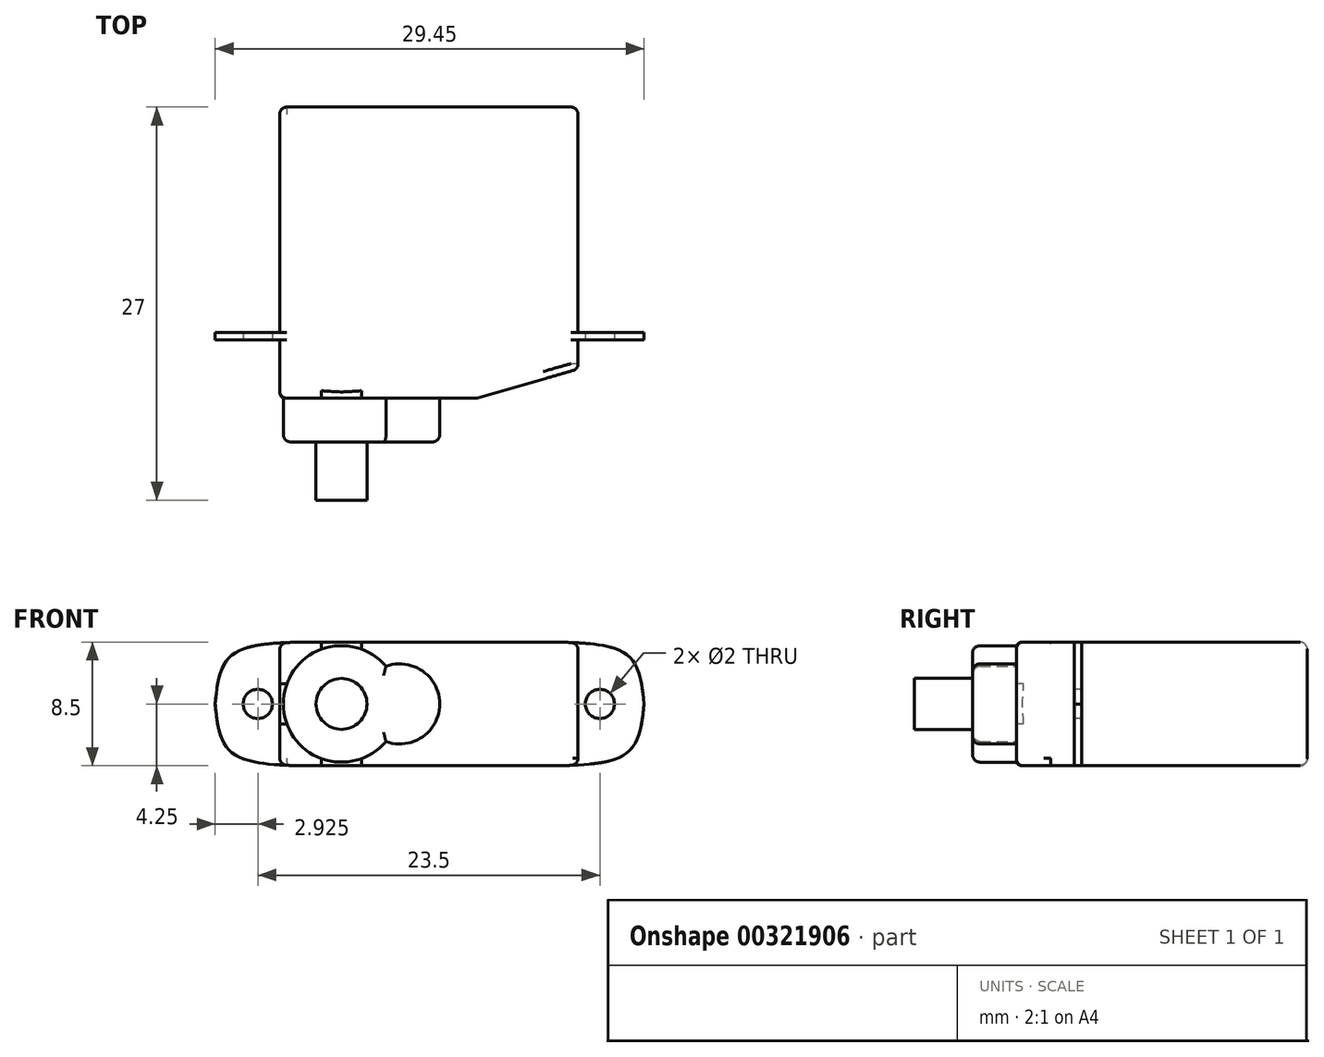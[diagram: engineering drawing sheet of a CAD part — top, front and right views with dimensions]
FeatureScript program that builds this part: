
annotation { "Feature Type Name" : "Feature", "Feature Type Description" : "" }
export const myFeature = defineFeature(function(context is Context, id is Id, definition is map)
    precondition{}
    {
        {
            var Q0;
            Q0=qCreatedBy(makeId("Top.planeOp"),FACE);
            var sketch = newSketch(context, id + "F0", { "sketchPlane" : qUnion([Q0])});
            skLineSegment(sketch, "E0.bottom", {"start": v(-30.64, 3) * mm, "end": v(-10.14, 3) * mm});
            skLineSegment(sketch, "E0.top", {"start": v(-30.64, -17) * mm, "end": v(-17.14, -17) * mm});
            skLineSegment(sketch, "E0.left", {"start": v(-30.64, 3) * mm, "end": v(-30.64, -17) * mm});
            skLineSegment(sketch, "E0.right", {"start": v(-10.14, 3) * mm, "end": v(-10.14, -15) * mm});
            skLineSegment(sketch, "E1", {"start": v(-17.14, -17) * mm, "end": v(-10.14, -15) * mm});
            skLineSegment(sketch, "E2.bottom", {"start": v(-30.64, -13) * mm, "end": v(-35.14, -13) * mm});
            skLineSegment(sketch, "E2.top", {"start": v(-30.64, -12.5) * mm, "end": v(-35.14, -12.5) * mm});
            skLineSegment(sketch, "E2.right", {"start": v(-35.14, -13) * mm, "end": v(-35.14, -12.5) * mm});
            skPoint(sketch, "E3.firstSnap0", {"position": v(-32.9, -12.5) * mm});
            skLineSegment(sketch, "E3.bottom", {"start": v(-10.14, -12.5) * mm, "end": v(-5.54, -12.5) * mm});
            skLineSegment(sketch, "E3.top", {"start": v(-10.14, -13) * mm, "end": v(-5.54, -13) * mm});
            skLineSegment(sketch, "E3.right", {"start": v(-5.54, -12.5) * mm, "end": v(-5.54, -13) * mm});
            skSolve(sketch);
        }
        {
            var Q0;
            {var subQ3=sQuery(id+"F0.wireOp",EDGE,"E0.bottom");Q0=makeQuery(id+"F0.imprint","IMPRINT",FACE,{"disambiguationData":[TD([[makeQuery(id+"F0.imprint","IMPRINT",EDGE,{"derivedFrom":subQ3}),-1.0]])]});}
            var Q1;
            {var subQ0=sQuery(id+"F0.wireOp",EDGE,"E2.bottom");Q1=makeQuery(id+"F0.imprint","IMPRINT",FACE,{"disambiguationData":[TD([[makeQuery(id+"F0.imprint","IMPRINT",EDGE,{"derivedFrom":subQ0}),-1.0]])]});}
            var Q2;
            {var subQ0=sQuery(id+"F0.wireOp",EDGE,"E3.bottom");Q2=makeQuery(id+"F0.imprint","IMPRINT",FACE,{"disambiguationData":[TD([[makeQuery(id+"F0.imprint","IMPRINT",EDGE,{"derivedFrom":subQ0}),-1.0]])]});}
            extrude(context, id + "F1", {"entities" : qUnion([Q0, Q1, Q2]), "depth" : 8.5 * mm});
        }
        {
            var Q0;
            Q0=makeQuery(id+"F1.opExtrude","SWEPT_FACE",FACE,{"disambiguationData":[OSD([sQuery(id+"F0.wireOp",EDGE,"E0.top")])]});
            var sketch = newSketch(context, id + "F2", { "sketchPlane" : qUnion([Q0])});
            skArc(sketch, "E4", {"start": v(-23.34, 6.83) * mm, "mid": v(-30.4, 4.25) * mm, "end": v(-23.34, 1.67) * mm});
            skPoint(sketch, "E4.centerSnap0", {"position": v(-30.64, 4.25) * mm});
            skArc(sketch, "E5", {"start": v(-23.34, 1.67) * mm, "mid": v(-19.64, 4.25) * mm, "end": v(-23.34, 6.83) * mm});
            skSolve(sketch);
        }
        {
            var Q0;
            {var subQ0=sQuery(id+"F2.wireOp",EDGE,"E5");Q0=makeQuery(id+"F2.imprint","IMPRINT",FACE,{"disambiguationData":[TD([[makeQuery(id+"F2.imprint","IMPRINT",EDGE,{"derivedFrom":subQ0}),1.0]])]});}
            extrude(context, id + "F3", {"entities" : qUnion([Q0]), "operationType" : NewBodyOperationType.ADD, "depth" : 3 * mm});
        }
        {
            var Q0;
            Q0=makeQuery(id+"F3.opExtrude","CAP_FACE",FACE,{"disambiguationData":[OSD([sQuery(id+"F2.wireOp",EDGE,"E4"),sQuery(id+"F2.wireOp",EDGE,"E5")])],"isStart":false});
            var sketch = newSketch(context, id + "F4", { "sketchPlane" : qUnion([Q0])});
            skCircle(sketch, "E6", {"center": v(-26.4, 4.25) * mm, "radius": 1.75 * mm});
            skSolve(sketch);
        }
        {
            var Q0;
            Q0=makeQuery(id+"F4.imprint","IMPRINT",FACE,{"disambiguationData":[TD([[makeQuery(id+"F4.imprint","IMPRINT",EDGE,{"derivedFrom":sQuery(id+"F4.wireOp",EDGE,"E6")}),1.0]])]});
            extrude(context, id + "F5", {"entities" : qUnion([Q0]), "operationType" : NewBodyOperationType.ADD, "depth" : 4 * mm});
        }
        {
            var Q0;
            Q0=makeQuery(id+"F1.opExtrude","SWEPT_FACE",FACE,{"disambiguationData":[OSD([sQuery(id+"F0.wireOp",EDGE,"E2.bottom")])]});
            var sketch = newSketch(context, id + "F6", { "sketchPlane" : qUnion([Q0])});
            skCircle(sketch, "E7", {"center": v(-32.14, 4.25) * mm, "radius": 1 * mm});
            skPoint(sketch, "E7.centerSnap0", {"position": v(-35.14, 4.25) * mm});
            skCircle(sketch, "E8", {"center": v(-8.64, 4.25) * mm, "radius": 1 * mm});
            skSolve(sketch);
        }
        {
            var Q0;
            Q0=makeQuery(id+"F6.imprint","IMPRINT",FACE,{"disambiguationData":[TD([[makeQuery(id+"F6.imprint","IMPRINT",EDGE,{"derivedFrom":sQuery(id+"F6.wireOp",EDGE,"E7")}),1.0]])]});
            var Q1;
            Q1=makeQuery(id+"F6.imprint","IMPRINT",FACE,{"disambiguationData":[TD([[makeQuery(id+"F6.imprint","IMPRINT",EDGE,{"derivedFrom":sQuery(id+"F6.wireOp",EDGE,"E8")}),1.0]])]});
            extrude(context, id + "F7", {"entities" : qUnion([Q0, Q1]), "operationType" : NewBodyOperationType.REMOVE, "oppositeDirection" : true, "depth" : 25 * mm});
        }
        {
            var Q0;
            Q0=makeQuery(id+"F1.opExtrude","CAP_EDGE",EDGE,{"disambiguationData":[OSD([sQuery(id+"F0.wireOp",EDGE,"E2.right")])],"isStart":false});
            var Q1;
            Q1=makeQuery(id+"F1.opExtrude","CAP_EDGE",EDGE,{"disambiguationData":[OSD([sQuery(id+"F0.wireOp",EDGE,"E2.right")])],"isStart":true});
            var Q2;
            Q2=makeQuery(id+"F1.opExtrude","CAP_EDGE",EDGE,{"disambiguationData":[OSD([sQuery(id+"F0.wireOp",EDGE,"E3.right")])],"isStart":false});
            var Q3;
            Q3=makeQuery(id+"F1.opExtrude","CAP_EDGE",EDGE,{"disambiguationData":[OSD([sQuery(id+"F0.wireOp",EDGE,"E3.right")])],"isStart":true});
            fillet(context, id + "F8", {"entities" : qUnion([Q0, Q1, Q2, Q3]), "radius" : 7 * mm, "rho" : 0.7, "crossSection" : FilletCrossSection.CONIC, "allowEdgeOverflow" : false});
        }
        {
            var Q0;
            {var subQ0=sQuery(id+"F0.wireOp",EDGE,"E0.left");Q0=makeQuery(id+"F8.opFillet","BLEND_EDGE",EDGE,{"blendedFrom":[makeQuery(id+"F1.opExtrude","CAP_EDGE",EDGE,{"disambiguationData":[OSD([sQuery(id+"F0.wireOp",EDGE,"E2.right")])],"isStart":false}),makeQuery(id+"F1.opExtrude","SWEPT_FACE",FACE,{"disambiguationData":[OSD([subQ0]),TDD([makeQuery(id+"F0.imprint","IMPRINT",EDGE,{"disambiguationData":[TD([[makeQuery(id+"F0.imprint","INTERSECT",VERTEX,{"derivedFrom":[sQuery(id+"F0.wireOp",EDGE,"E0.bottom"),subQ0]}),-1.0]])],"derivedFrom":subQ0})])]})],"blendedInto":[makeQuery(id+"F1.opExtrude","SWEPT_FACE",FACE,{"disambiguationData":[OSD([subQ0]),TDD([makeQuery(id+"F0.imprint","IMPRINT",EDGE,{"disambiguationData":[TD([[makeQuery(id+"F0.imprint","INTERSECT",VERTEX,{"derivedFrom":[sQuery(id+"F0.wireOp",EDGE,"E0.bottom"),subQ0]}),-1.0]])],"derivedFrom":subQ0})])]})]});}
            var Q1;
            {var subQ0=sQuery(id+"F0.wireOp",EDGE,"E0.left");Q1=makeQuery(id+"F8.opFillet","BLEND_EDGE",EDGE,{"blendedFrom":[makeQuery(id+"F1.opExtrude","CAP_EDGE",EDGE,{"disambiguationData":[OSD([sQuery(id+"F0.wireOp",EDGE,"E2.right")])],"isStart":false}),makeQuery(id+"F1.opExtrude","SWEPT_FACE",FACE,{"disambiguationData":[OSD([subQ0]),TDD([makeQuery(id+"F0.imprint","IMPRINT",EDGE,{"disambiguationData":[TD([[makeQuery(id+"F0.imprint","INTERSECT",VERTEX,{"derivedFrom":[sQuery(id+"F0.wireOp",EDGE,"E0.top"),subQ0]}),1.0]])],"derivedFrom":subQ0})])]})],"blendedInto":[makeQuery(id+"F1.opExtrude","SWEPT_FACE",FACE,{"disambiguationData":[OSD([subQ0]),TDD([makeQuery(id+"F0.imprint","IMPRINT",EDGE,{"disambiguationData":[TD([[makeQuery(id+"F0.imprint","INTERSECT",VERTEX,{"derivedFrom":[sQuery(id+"F0.wireOp",EDGE,"E0.top"),subQ0]}),1.0]])],"derivedFrom":subQ0})])]})]});}
            var Q2;
            {var subQ0=sQuery(id+"F0.wireOp",EDGE,"E0.left");Q2=makeQuery(id+"F8.opFillet","BLEND_EDGE",EDGE,{"blendedFrom":[makeQuery(id+"F1.opExtrude","CAP_EDGE",EDGE,{"disambiguationData":[OSD([sQuery(id+"F0.wireOp",EDGE,"E2.right")])],"isStart":true}),makeQuery(id+"F1.opExtrude","SWEPT_FACE",FACE,{"disambiguationData":[OSD([subQ0]),TDD([makeQuery(id+"F0.imprint","IMPRINT",EDGE,{"disambiguationData":[TD([[makeQuery(id+"F0.imprint","INTERSECT",VERTEX,{"derivedFrom":[sQuery(id+"F0.wireOp",EDGE,"E0.top"),subQ0]}),1.0]])],"derivedFrom":subQ0})])]})],"blendedInto":[makeQuery(id+"F1.opExtrude","SWEPT_FACE",FACE,{"disambiguationData":[OSD([subQ0]),TDD([makeQuery(id+"F0.imprint","IMPRINT",EDGE,{"disambiguationData":[TD([[makeQuery(id+"F0.imprint","INTERSECT",VERTEX,{"derivedFrom":[sQuery(id+"F0.wireOp",EDGE,"E0.top"),subQ0]}),1.0]])],"derivedFrom":subQ0})])]})]});}
            var Q3;
            {var subQ0=sQuery(id+"F0.wireOp",EDGE,"E0.left");Q3=makeQuery(id+"F8.opFillet","BLEND_EDGE",EDGE,{"blendedFrom":[makeQuery(id+"F1.opExtrude","CAP_EDGE",EDGE,{"disambiguationData":[OSD([sQuery(id+"F0.wireOp",EDGE,"E2.right")])],"isStart":true}),makeQuery(id+"F1.opExtrude","SWEPT_FACE",FACE,{"disambiguationData":[OSD([subQ0]),TDD([makeQuery(id+"F0.imprint","IMPRINT",EDGE,{"disambiguationData":[TD([[makeQuery(id+"F0.imprint","INTERSECT",VERTEX,{"derivedFrom":[sQuery(id+"F0.wireOp",EDGE,"E0.bottom"),subQ0]}),-1.0]])],"derivedFrom":subQ0})])]})],"blendedInto":[makeQuery(id+"F1.opExtrude","SWEPT_FACE",FACE,{"disambiguationData":[OSD([subQ0]),TDD([makeQuery(id+"F0.imprint","IMPRINT",EDGE,{"disambiguationData":[TD([[makeQuery(id+"F0.imprint","INTERSECT",VERTEX,{"derivedFrom":[sQuery(id+"F0.wireOp",EDGE,"E0.bottom"),subQ0]}),-1.0]])],"derivedFrom":subQ0})])]})]});}
            var Q4;
            Q4=makeQuery(id+"F1.opExtrude","CAP_EDGE",EDGE,{"disambiguationData":[OSD([sQuery(id+"F0.wireOp",EDGE,"E0.bottom")])],"isStart":true});
            var Q5;
            Q5=makeQuery(id+"F1.opExtrude","SWEPT_EDGE",EDGE,{"disambiguationData":[OSD([sQuery(id+"F0.wireOp",EDGE,"E0.bottom"),sQuery(id+"F0.wireOp",EDGE,"E0.left")])]});
            var Q6;
            Q6=makeQuery(id+"F1.opExtrude","CAP_EDGE",EDGE,{"disambiguationData":[OSD([sQuery(id+"F0.wireOp",EDGE,"E0.bottom")])],"isStart":false});
            var Q7;
            Q7=makeQuery(id+"F1.opExtrude","SWEPT_EDGE",EDGE,{"disambiguationData":[OSD([sQuery(id+"F0.wireOp",EDGE,"E0.bottom"),sQuery(id+"F0.wireOp",EDGE,"E0.right")])]});
            var Q8;
            {var subQ0=sQuery(id+"F0.wireOp",EDGE,"E0.right");Q8=makeQuery(id+"F8.opFillet","BLEND_EDGE",EDGE,{"blendedFrom":[makeQuery(id+"F1.opExtrude","CAP_EDGE",EDGE,{"disambiguationData":[OSD([sQuery(id+"F0.wireOp",EDGE,"E3.right")])],"isStart":true}),makeQuery(id+"F1.opExtrude","SWEPT_FACE",FACE,{"disambiguationData":[OSD([subQ0]),TDD([makeQuery(id+"F0.imprint","IMPRINT",EDGE,{"disambiguationData":[TD([[makeQuery(id+"F0.imprint","INTERSECT",VERTEX,{"derivedFrom":[sQuery(id+"F0.wireOp",EDGE,"E0.bottom"),subQ0]}),-1.0]])],"derivedFrom":subQ0})])]})],"blendedInto":[makeQuery(id+"F1.opExtrude","SWEPT_FACE",FACE,{"disambiguationData":[OSD([subQ0]),TDD([makeQuery(id+"F0.imprint","IMPRINT",EDGE,{"disambiguationData":[TD([[makeQuery(id+"F0.imprint","INTERSECT",VERTEX,{"derivedFrom":[sQuery(id+"F0.wireOp",EDGE,"E0.bottom"),subQ0]}),-1.0]])],"derivedFrom":subQ0})])]})]});}
            var Q9;
            {var subQ0=sQuery(id+"F0.wireOp",EDGE,"E0.right");Q9=makeQuery(id+"F8.opFillet","BLEND_EDGE",EDGE,{"blendedFrom":[makeQuery(id+"F1.opExtrude","CAP_EDGE",EDGE,{"disambiguationData":[OSD([sQuery(id+"F0.wireOp",EDGE,"E3.right")])],"isStart":false}),makeQuery(id+"F1.opExtrude","SWEPT_FACE",FACE,{"disambiguationData":[OSD([subQ0]),TDD([makeQuery(id+"F0.imprint","IMPRINT",EDGE,{"disambiguationData":[TD([[makeQuery(id+"F0.imprint","INTERSECT",VERTEX,{"derivedFrom":[sQuery(id+"F0.wireOp",EDGE,"E0.bottom"),subQ0]}),-1.0]])],"derivedFrom":subQ0})])]})],"blendedInto":[makeQuery(id+"F1.opExtrude","SWEPT_FACE",FACE,{"disambiguationData":[OSD([subQ0]),TDD([makeQuery(id+"F0.imprint","IMPRINT",EDGE,{"disambiguationData":[TD([[makeQuery(id+"F0.imprint","INTERSECT",VERTEX,{"derivedFrom":[sQuery(id+"F0.wireOp",EDGE,"E0.bottom"),subQ0]}),-1.0]])],"derivedFrom":subQ0})])]})]});}
            var Q10;
            {var subQ0=sQuery(id+"F0.wireOp",EDGE,"E0.right");Q10=makeQuery(id+"F8.opFillet","BLEND_EDGE",EDGE,{"blendedFrom":[makeQuery(id+"F1.opExtrude","CAP_EDGE",EDGE,{"disambiguationData":[OSD([sQuery(id+"F0.wireOp",EDGE,"E3.right")])],"isStart":false}),makeQuery(id+"F1.opExtrude","SWEPT_FACE",FACE,{"disambiguationData":[OSD([subQ0]),TDD([makeQuery(id+"F0.imprint","IMPRINT",EDGE,{"disambiguationData":[TD([[makeQuery(id+"F0.imprint","INTERSECT",VERTEX,{"derivedFrom":[subQ0,sQuery(id+"F0.wireOp",EDGE,"E1")]}),1.0]])],"derivedFrom":subQ0})])]})],"blendedInto":[makeQuery(id+"F1.opExtrude","SWEPT_FACE",FACE,{"disambiguationData":[OSD([subQ0]),TDD([makeQuery(id+"F0.imprint","IMPRINT",EDGE,{"disambiguationData":[TD([[makeQuery(id+"F0.imprint","INTERSECT",VERTEX,{"derivedFrom":[subQ0,sQuery(id+"F0.wireOp",EDGE,"E1")]}),1.0]])],"derivedFrom":subQ0})])]})]});}
            var Q11;
            {var subQ0=sQuery(id+"F0.wireOp",EDGE,"E0.right");Q11=makeQuery(id+"F8.opFillet","BLEND_EDGE",EDGE,{"blendedFrom":[makeQuery(id+"F1.opExtrude","CAP_EDGE",EDGE,{"disambiguationData":[OSD([sQuery(id+"F0.wireOp",EDGE,"E3.right")])],"isStart":true}),makeQuery(id+"F1.opExtrude","SWEPT_FACE",FACE,{"disambiguationData":[OSD([subQ0]),TDD([makeQuery(id+"F0.imprint","IMPRINT",EDGE,{"disambiguationData":[TD([[makeQuery(id+"F0.imprint","INTERSECT",VERTEX,{"derivedFrom":[subQ0,sQuery(id+"F0.wireOp",EDGE,"E1")]}),1.0]])],"derivedFrom":subQ0})])]})],"blendedInto":[makeQuery(id+"F1.opExtrude","SWEPT_FACE",FACE,{"disambiguationData":[OSD([subQ0]),TDD([makeQuery(id+"F0.imprint","IMPRINT",EDGE,{"disambiguationData":[TD([[makeQuery(id+"F0.imprint","INTERSECT",VERTEX,{"derivedFrom":[subQ0,sQuery(id+"F0.wireOp",EDGE,"E1")]}),1.0]])],"derivedFrom":subQ0})])]})]});}
            var Q12;
            Q12=makeQuery(id+"F1.opExtrude","SWEPT_EDGE",EDGE,{"disambiguationData":[OSD([sQuery(id+"F0.wireOp",EDGE,"E0.right"),sQuery(id+"F0.wireOp",EDGE,"E1")])]});
            var Q13;
            Q13=makeQuery(id+"F1.opExtrude","CAP_EDGE",EDGE,{"disambiguationData":[OSD([sQuery(id+"F0.wireOp",EDGE,"E1")])],"isStart":false});
            var Q14;
            Q14=makeQuery(id+"F1.opExtrude","CAP_EDGE",EDGE,{"disambiguationData":[OSD([sQuery(id+"F0.wireOp",EDGE,"E1")])],"isStart":true});
            var Q15;
            Q15=makeQuery(id+"F1.opExtrude","SWEPT_EDGE",EDGE,{"disambiguationData":[OSD([sQuery(id+"F0.wireOp",EDGE,"E0.top"),sQuery(id+"F0.wireOp",EDGE,"E1")])]});
            var Q16;
            {var subQ0=sQuery(id+"F0.wireOp",EDGE,"E2.bottom");var subQ1=sQuery(id+"F0.wireOp",EDGE,"E0.left");var subQ2=sQuery(id+"F0.wireOp",EDGE,"E0.top");Q16=makeQuery(id+"F3.boolean.opBoolean","SPLIT",EDGE,{"disambiguationData":[TD([makeQuery(id+"F1.opExtrude","CAP_FACE",FACE,{"disambiguationData":[OSD([sQuery(id+"F0.wireOp",EDGE,"E0.bottom"),subQ2,subQ1,sQuery(id+"F0.wireOp",EDGE,"E0.right"),sQuery(id+"F0.wireOp",EDGE,"E1"),subQ0,sQuery(id+"F0.wireOp",EDGE,"E2.top"),sQuery(id+"F0.wireOp",EDGE,"E2.right"),sQuery(id+"F0.wireOp",EDGE,"E3.bottom"),sQuery(id+"F0.wireOp",EDGE,"E3.top"),sQuery(id+"F0.wireOp",EDGE,"E3.right")])],"isStart":true})])],"derivedFrom":makeQuery(id+"F1.opExtrude","SWEPT_EDGE",EDGE,{"disambiguationData":[OSD([subQ2,subQ1])]})});}
            var Q17;
            {var subQ0=sQuery(id+"F0.wireOp",EDGE,"E1");var subQ1=sQuery(id+"F0.wireOp",EDGE,"E0.top");Q17=makeQuery(id+"F3.boolean.opBoolean","SPLIT",EDGE,{"disambiguationData":[TD([makeQuery(id+"F1.opExtrude","SWEPT_FACE",FACE,{"disambiguationData":[OSD([subQ0])]})])],"derivedFrom":makeQuery(id+"F1.opExtrude","CAP_EDGE",EDGE,{"disambiguationData":[OSD([subQ1])],"isStart":true})});}
            var Q18;
            {var subQ0=sQuery(id+"F0.wireOp",EDGE,"E1");var subQ1=sQuery(id+"F0.wireOp",EDGE,"E0.top");Q18=makeQuery(id+"F3.boolean.opBoolean","SPLIT",EDGE,{"disambiguationData":[TD([makeQuery(id+"F1.opExtrude","SWEPT_FACE",FACE,{"disambiguationData":[OSD([subQ0])]})])],"derivedFrom":makeQuery(id+"F1.opExtrude","CAP_EDGE",EDGE,{"disambiguationData":[OSD([subQ1])],"isStart":false})});}
            var Q19;
            Q19=makeQuery(id+"F3.opExtrude","CAP_EDGE",EDGE,{"disambiguationData":[OSD([sQuery(id+"F2.wireOp",EDGE,"E4")])],"isStart":false});
            var Q20;
            Q20=makeQuery(id+"F3.opExtrude","CAP_EDGE",EDGE,{"disambiguationData":[OSD([sQuery(id+"F2.wireOp",EDGE,"E5")])],"isStart":false});
            fillet(context, id + "F9", {"entities" : qUnion([Q0, Q1, Q2, Q3, Q4, Q5, Q6, Q7, Q8, Q9, Q10, Q11, Q12, Q13, Q14, Q15, Q16, Q17, Q18, Q19, Q20]), "radius" : 0.5 * mm, "tangentPropagation" : true, "allowEdgeOverflow" : false});
        }
    });
